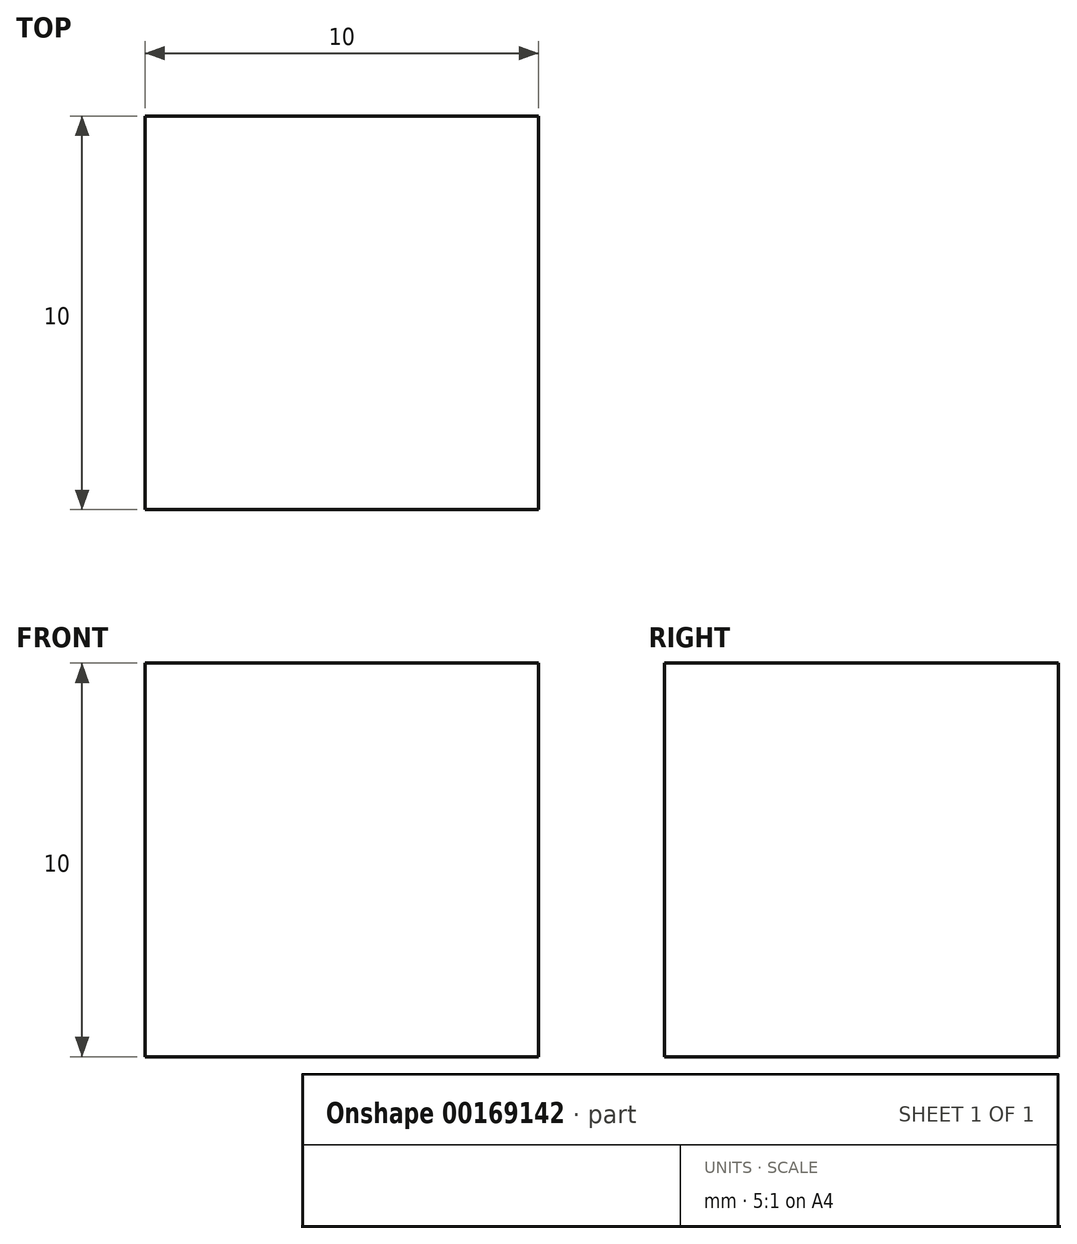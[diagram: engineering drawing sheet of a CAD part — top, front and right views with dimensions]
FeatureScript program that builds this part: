
annotation { "Feature Type Name" : "Feature", "Feature Type Description" : "" }
export const myFeature = defineFeature(function(context is Context, id is Id, definition is map)
    precondition{}
    {
        {
            var Q0;
            Q0=qCreatedBy(makeId("Top.planeOp"),FACE);
            var sketch = newSketch(context, id + "F0", { "sketchPlane" : qUnion([Q0])});
            skLineSegment(sketch, "E0.bottom", {"start": v(0, 0) * mm, "end": v(10, 0) * mm});
            skLineSegment(sketch, "E0.top", {"start": v(0, -10) * mm, "end": v(10, -10) * mm});
            skLineSegment(sketch, "E0.left", {"start": v(0, 0) * mm, "end": v(0, -10) * mm});
            skLineSegment(sketch, "E0.right", {"start": v(10, 0) * mm, "end": v(10, -10) * mm});
            skSolve(sketch);
        }
        {
            var Q0;
            Q0=makeQuery(id+"F0.imprint","IMPRINT",FACE,{"disambiguationData":[TD([[makeQuery(id+"F0.imprint","IMPRINT",EDGE,{"derivedFrom":sQuery(id+"F0.wireOp",EDGE,"E0.bottom")}),-1.0]])]});
            extrude(context, id + "F1", {"entities" : qUnion([Q0]), "depth" : 10 * mm});
        }
    });
